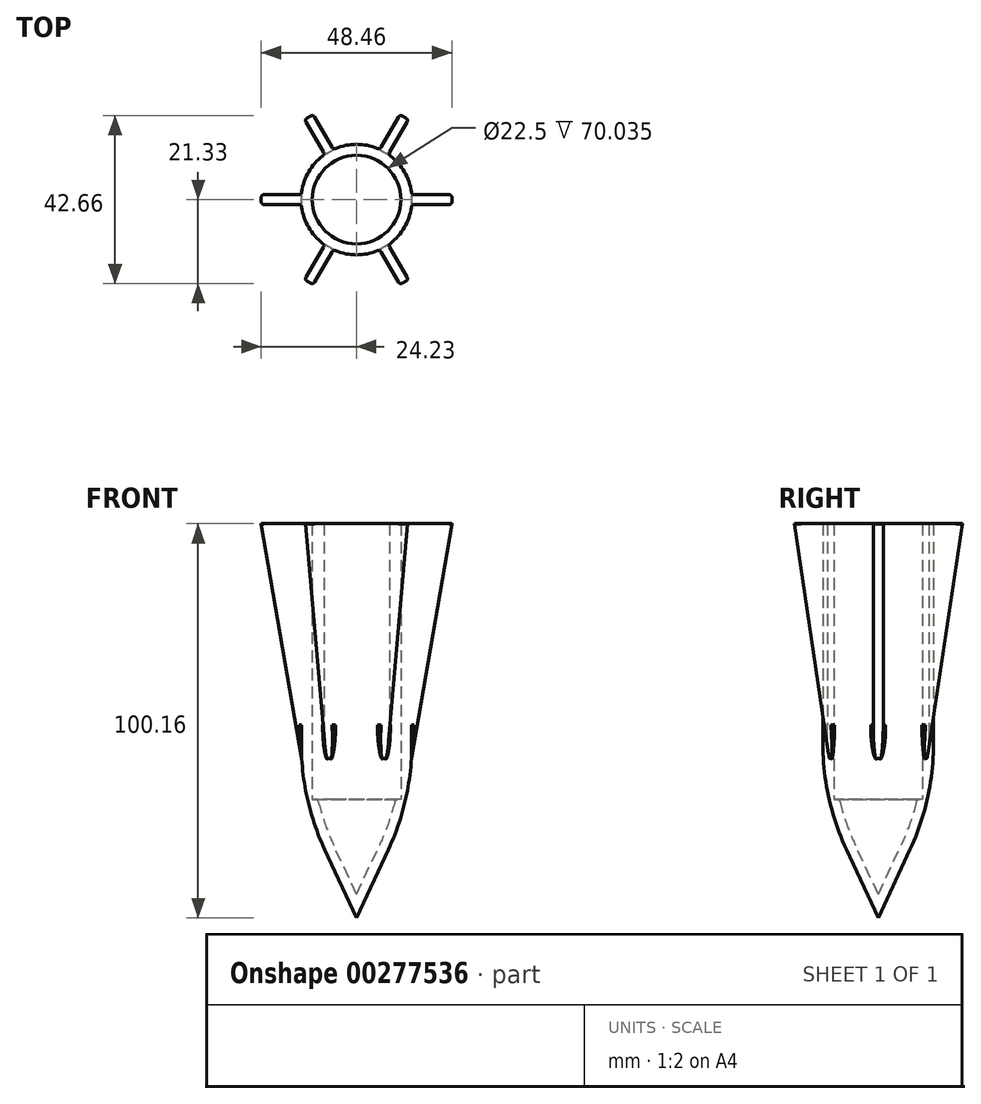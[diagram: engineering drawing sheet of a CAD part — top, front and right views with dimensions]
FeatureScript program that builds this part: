
annotation { "Feature Type Name" : "Feature", "Feature Type Description" : "" }
export const myFeature = defineFeature(function(context is Context, id is Id, definition is map)
    precondition{}
    {
        {
            var Q0;
            Q0=qCreatedBy(makeId("Top.planeOp"),FACE);
            var sketch = newSketch(context, id + "F0", { "sketchPlane" : qUnion([Q0])});
            skCircle(sketch, "E0", {"center": v(0, 0) * mm, "radius": 11.25 * mm});
            skCircle(sketch, "E1", {"center": v(0, 0) * mm, "radius": 14.04 * mm});
            skSolve(sketch);
        }
        {
            var Q0;
            Q0=makeQuery(id+"F0.imprint","IMPRINT",FACE,{"disambiguationData":[TD([[makeQuery(id+"F0.imprint","IMPRINT",EDGE,{"derivedFrom":sQuery(id+"F0.wireOp",EDGE,"E0")}),-1.0]])]});
            extrude(context, id + "F1", {"entities" : qUnion([Q0]), "depth" : 50.8 * mm});
        }
        {
            var Q0;
            Q0=makeQuery(id+"F0.imprint","IMPRINT",FACE,{"disambiguationData":[TD([[makeQuery(id+"F0.imprint","IMPRINT",EDGE,{"derivedFrom":sQuery(id+"F0.wireOp",EDGE,"E0")}),-1.0]])]});
            var Q1;
            Q1=makeQuery(id+"F0.imprint","IMPRINT",FACE,{"disambiguationData":[TD([[makeQuery(id+"F0.imprint","IMPRINT",EDGE,{"derivedFrom":sQuery(id+"F0.wireOp",EDGE,"E0")}),1.0]])]});
            extrude(context, id + "F2", {"entities" : qUnion([Q0, Q1]), "operationType" : NewBodyOperationType.ADD, "oppositeDirection" : true, "depth" : 31.75 * mm, "hasDraft" : true, "draftAngle" : 25 * degree, "draftPullDirection" : true});
        }
        {
            var Q0;
            {var subQ0=sQuery(id+"F0.wireOp",EDGE,"E1");Q0=makeQuery(id+"F2.boolean.opBoolean","MERGE",EDGE,{"derivedFrom":[makeQuery(id+"F1.opExtrude","CAP_EDGE",EDGE,{"disambiguationData":[OSD([subQ0])],"isStart":true}),makeQuery(id+"F2.opExtrude","CAP_EDGE",EDGE,{"disambiguationData":[OSD([subQ0])],"isStart":true})]});}
            fillet(context, id + "F3", {"entities" : qUnion([Q0]), "radius" : 63.5 * mm, "tangentPropagation" : true, "allowEdgeOverflow" : false});
        }
        {
            var Q0;
            Q0=makeQuery(id+"F2.opExtrude","CAP_FACE",FACE,{"disambiguationData":[OSD([sQuery(id+"F0.wireOp",EDGE,"E1")])],"isStart":true});
            shell(context, id + "F4", {"entities" : qUnion([Q0]), "thickness" : 2.54 * mm});
        }
        {
            var Q0;
            {var subQ0=sQuery(id+"F0.wireOp",EDGE,"E1");Q0=makeQuery(id+"F4.opShell","TWEAK_EDGE",EDGE,{"derivedFrom":[makeQuery(id+"F2.opExtrude","CAP_FACE",FACE,{"disambiguationData":[OSD([subQ0])],"isStart":true}),makeQuery(id+"F3.opFillet","BLEND_FACE",FACE,{"disambiguationData":[OSD([subQ0])]})]});}
            fillet(context, id + "F5", {"entities" : qUnion([Q0]), "radius" : 0.76 * mm, "tangentPropagation" : true, "allowEdgeOverflow" : false});
        }
        {
            var Q0;
            Q0=qCreatedBy(makeId("Front.planeOp"),FACE);
            var sketch = newSketch(context, id + "F6", { "sketchPlane" : qUnion([Q0])});
            skLineSegment(sketch, "E2", {"start": v(12.94, 4.62) * mm, "end": v(24.23, 69.93) * mm});
            skLineSegment(sketch, "E3", {"start": v(24.23, 69.93) * mm, "end": v(11.52, 69.93) * mm});
            skLineSegment(sketch, "E4", {"start": v(11.52, 69.93) * mm, "end": v(12.94, 4.62) * mm});
            skSolve(sketch);
        }
        {
            var Q0;
            Q0=makeQuery(id+"F6.imprint","IMPRINT",FACE,{"disambiguationData":[TD([[makeQuery(id+"F6.imprint","IMPRINT",EDGE,{"derivedFrom":sQuery(id+"F6.wireOp",EDGE,"E2")}),1.0]])]});
            extrude(context, id + "F7", {"entities" : qUnion([Q0]), "operationType" : NewBodyOperationType.ADD, "endBound" : BoundingType.SYMMETRIC, "depth" : 2.54 * mm});
        }
        {
            var Q0;
            Q0=makeQuery(id+"F7.opExtrude","CAP_EDGE",EDGE,{"disambiguationData":[OSD([sQuery(id+"F6.wireOp",EDGE,"E2")])],"isStart":false});
            var Q1;
            Q1=makeQuery(id+"F7.opExtrude","CAP_EDGE",EDGE,{"disambiguationData":[OSD([sQuery(id+"F6.wireOp",EDGE,"E2")])],"isStart":true});
            fillet(context, id + "F8", {"entities" : qUnion([Q0, Q1]), "radius" : 0.76 * mm, "tangentPropagation" : true, "allowEdgeOverflow" : false});
        }
        {
            var Q0;
            Q0=makeQuery(id+"F7.boolean.opBoolean","INTERSECT",EDGE,{"derivedFrom":[makeQuery(id+"F1.opExtrude","SWEPT_FACE",FACE,{"disambiguationData":[OSD([sQuery(id+"F0.wireOp",EDGE,"E1")])]}),makeQuery(id+"F7.opExtrude","CAP_FACE",FACE,{"disambiguationData":[OSD([sQuery(id+"F6.wireOp",EDGE,"E2"),sQuery(id+"F6.wireOp",EDGE,"E3"),sQuery(id+"F6.wireOp",EDGE,"E4")])],"isStart":true})]});
            fillet(context, id + "F9", {"entities" : qUnion([Q0]), "radius" : 0.72 * mm, "tangentPropagation" : true, "allowEdgeOverflow" : false});
        }
        {
            var Q0;
            Q0=qCreatedBy(makeId("Front.planeOp"),FACE);
            var sketch = newSketch(context, id + "F10", { "sketchPlane" : qUnion([Q0])});
            skLineSegment(sketch, "E5", {"start": v(0, 0) * mm, "end": v(0, 21.59) * mm});
            skSolve(sketch);
        }
        {
            var Q0;
            Q0=makeQuery(id+"F1.opExtrude","SWEPT_BODY",BODY,{"disambiguationData":[OSD([sQuery(id+"F0.wireOp",EDGE,"E0"),sQuery(id+"F0.wireOp",EDGE,"E1")])]});
            var Q1;
            Q1=sQuery(id+"F10.wireOp",EDGE,"E5");
            circularPattern(context, id + "F11", {"entities" : qUnion([Q0]), "axis" : qUnion([Q1]), "angle" : 360 * degree, "instanceCount" : 6, "equalSpace" : true});
        }
        {
            var Q0;
            Q0=makeQuery(id+"F11.opPattern","COPY",BODY,{"derivedFrom":makeQuery(id+"F1.opExtrude","SWEPT_BODY",BODY,{"disambiguationData":[OSD([sQuery(id+"F0.wireOp",EDGE,"E0"),sQuery(id+"F0.wireOp",EDGE,"E1")])]}),"instanceName":"2"});
            var Q1;
            Q1=makeQuery(id+"F11.opPattern","COPY",BODY,{"derivedFrom":makeQuery(id+"F1.opExtrude","SWEPT_BODY",BODY,{"disambiguationData":[OSD([sQuery(id+"F0.wireOp",EDGE,"E0"),sQuery(id+"F0.wireOp",EDGE,"E1")])]}),"instanceName":"1"});
            var Q2;
            Q2=makeQuery(id+"F1.opExtrude","SWEPT_BODY",BODY,{"disambiguationData":[OSD([sQuery(id+"F0.wireOp",EDGE,"E0"),sQuery(id+"F0.wireOp",EDGE,"E1")])]});
            var Q3;
            Q3=makeQuery(id+"F11.opPattern","COPY",BODY,{"derivedFrom":makeQuery(id+"F1.opExtrude","SWEPT_BODY",BODY,{"disambiguationData":[OSD([sQuery(id+"F0.wireOp",EDGE,"E0"),sQuery(id+"F0.wireOp",EDGE,"E1")])]}),"instanceName":"5"});
            var Q4;
            Q4=makeQuery(id+"F11.opPattern","COPY",BODY,{"derivedFrom":makeQuery(id+"F1.opExtrude","SWEPT_BODY",BODY,{"disambiguationData":[OSD([sQuery(id+"F0.wireOp",EDGE,"E0"),sQuery(id+"F0.wireOp",EDGE,"E1")])]}),"instanceName":"4"});
            var Q5;
            Q5=makeQuery(id+"F11.opPattern","COPY",BODY,{"derivedFrom":makeQuery(id+"F1.opExtrude","SWEPT_BODY",BODY,{"disambiguationData":[OSD([sQuery(id+"F0.wireOp",EDGE,"E0"),sQuery(id+"F0.wireOp",EDGE,"E1")])]}),"instanceName":"3"});
            booleanBodies(context, id + "F12", {"operationType" : BooleanOperationType.UNION, "tools" : qUnion([Q0, Q1, Q2, Q3, Q4, Q5])});
        }
        {
            var Q0;
            Q0=makeQuery(id+"F11.opPattern","COPY",FACE,{"derivedFrom":makeQuery(id+"F7.opExtrude","SWEPT_FACE",FACE,{"disambiguationData":[OSD([sQuery(id+"F6.wireOp",EDGE,"E3")])]}),"instanceName":"2"});
            var Q1;
            Q1=makeQuery(id+"F11.opPattern","COPY",FACE,{"derivedFrom":makeQuery(id+"F7.opExtrude","SWEPT_FACE",FACE,{"disambiguationData":[OSD([sQuery(id+"F6.wireOp",EDGE,"E3")])]}),"instanceName":"1"});
            var Q2;
            Q2=makeQuery(id+"F7.opExtrude","SWEPT_FACE",FACE,{"disambiguationData":[OSD([sQuery(id+"F6.wireOp",EDGE,"E3")])]});
            var Q3;
            Q3=makeQuery(id+"F11.opPattern","COPY",FACE,{"derivedFrom":makeQuery(id+"F7.opExtrude","SWEPT_FACE",FACE,{"disambiguationData":[OSD([sQuery(id+"F6.wireOp",EDGE,"E3")])]}),"instanceName":"5"});
            var Q4;
            Q4=makeQuery(id+"F11.opPattern","COPY",FACE,{"derivedFrom":makeQuery(id+"F7.opExtrude","SWEPT_FACE",FACE,{"disambiguationData":[OSD([sQuery(id+"F6.wireOp",EDGE,"E3")])]}),"instanceName":"4"});
            var Q5;
            Q5=makeQuery(id+"F11.opPattern","COPY",FACE,{"derivedFrom":makeQuery(id+"F7.opExtrude","SWEPT_FACE",FACE,{"disambiguationData":[OSD([sQuery(id+"F6.wireOp",EDGE,"E3")])]}),"instanceName":"3"});
            extrude(context, id + "F13", {"entities" : qUnion([Q0, Q1, Q2, Q3, Q4, Q5]), "operationType" : NewBodyOperationType.ADD, "depth" : 0.1 * mm});
        }
        {
            var Q0;
            {var subQ0=makeQuery(id+"F1.opExtrude","CAP_FACE",FACE,{"disambiguationData":[OSD([sQuery(id+"F0.wireOp",EDGE,"E0"),sQuery(id+"F0.wireOp",EDGE,"E1")])],"isStart":false});Q0=makeQuery(id+"F12.opBoolean","MERGE",FACE,{"derivedFrom":[subQ0,makeQuery(id+"F11.opPattern","COPY",FACE,{"derivedFrom":subQ0,"instanceName":"1"}),makeQuery(id+"F11.opPattern","COPY",FACE,{"derivedFrom":subQ0,"instanceName":"2"}),makeQuery(id+"F11.opPattern","COPY",FACE,{"derivedFrom":subQ0,"instanceName":"3"}),makeQuery(id+"F11.opPattern","COPY",FACE,{"derivedFrom":subQ0,"instanceName":"4"}),makeQuery(id+"F11.opPattern","COPY",FACE,{"derivedFrom":subQ0,"instanceName":"5"})]});}
            extrude(context, id + "F14", {"entities" : qUnion([Q0]), "operationType" : NewBodyOperationType.ADD, "depth" : 17.65 * mm});
        }
        {
            var Q0;
            Q0=makeQuery(id+"F14.opExtrude","CAP_FACE",FACE,{"disambiguationData":[OSD([sQuery(id+"F0.wireOp",EDGE,"E0"),sQuery(id+"F0.wireOp",EDGE,"E1")])],"isStart":false});
            extrude(context, id + "F15", {"entities" : qUnion([Q0]), "operationType" : NewBodyOperationType.ADD, "depth" : 1.58 * mm});
        }
    });
